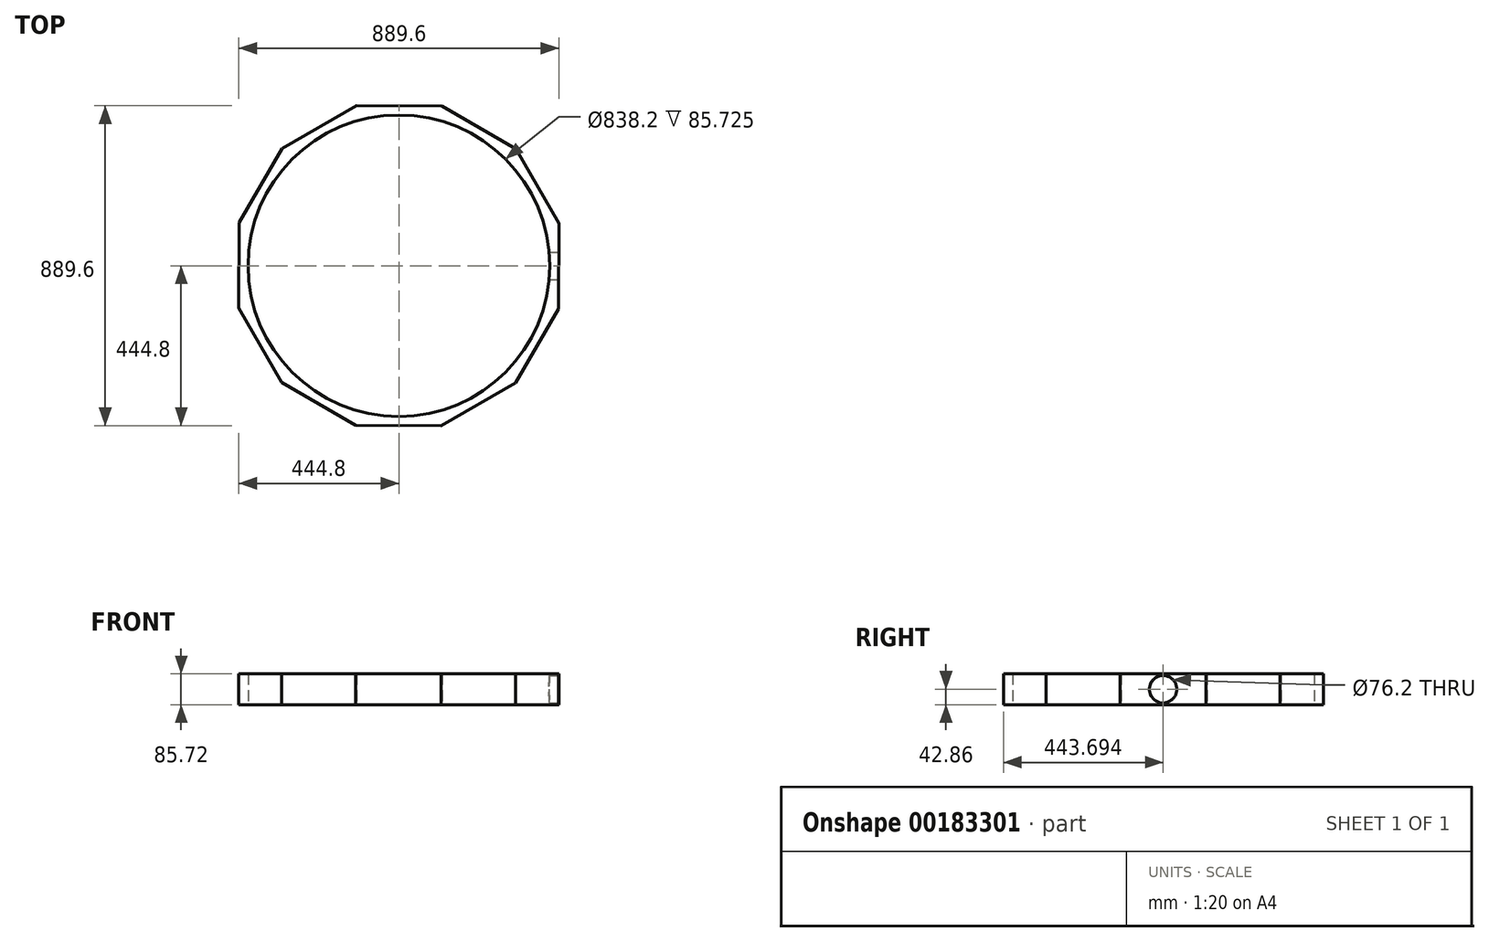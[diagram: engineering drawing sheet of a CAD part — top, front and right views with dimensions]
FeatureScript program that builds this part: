
annotation { "Feature Type Name" : "Feature", "Feature Type Description" : "" }
export const myFeature = defineFeature(function(context is Context, id is Id, definition is map)
    precondition{}
    {
        {
            var Q0;
            Q0=qCreatedBy(makeId("Top.planeOp"),FACE);
            var sketch = newSketch(context, id + "F0", { "sketchPlane" : qUnion([Q0])});
            skCircle(sketch, "E0.cCircle", {"center": v(0, 0) * mm, "radius": 444.5 * mm, "construction": true});
            skLineSegment(sketch, "E0.0", {"start": v(326.23, 324.56) * mm, "end": v(444.8, 117.97) * mm});
            skLineSegment(sketch, "E0.1", {"start": v(444.8, 117.97) * mm, "end": v(444.2, -120.24) * mm});
            skLineSegment(sketch, "E0.2", {"start": v(444.2, -120.24) * mm, "end": v(324.56, -326.23) * mm});
            skLineSegment(sketch, "E0.3", {"start": v(324.56, -326.23) * mm, "end": v(117.97, -444.8) * mm});
            skLineSegment(sketch, "E0.4", {"start": v(117.97, -444.8) * mm, "end": v(-120.24, -444.2) * mm});
            skLineSegment(sketch, "E0.5", {"start": v(-120.24, -444.2) * mm, "end": v(-326.23, -324.56) * mm});
            skLineSegment(sketch, "E0.6", {"start": v(-326.23, -324.56) * mm, "end": v(-444.8, -117.97) * mm});
            skLineSegment(sketch, "E0.7", {"start": v(-444.8, -117.97) * mm, "end": v(-444.2, 120.24) * mm});
            skLineSegment(sketch, "E0.8", {"start": v(-444.2, 120.24) * mm, "end": v(-324.56, 326.23) * mm});
            skLineSegment(sketch, "E0.9", {"start": v(-324.56, 326.23) * mm, "end": v(-117.97, 444.8) * mm});
            skLineSegment(sketch, "E0.10", {"start": v(-117.97, 444.8) * mm, "end": v(120.24, 444.2) * mm});
            skLineSegment(sketch, "E0.11", {"start": v(120.24, 444.2) * mm, "end": v(326.23, 324.56) * mm});
            skPoint(sketch, "E0.0.midPoint", {"position": v(385.52, 221.26) * mm});
            skCircle(sketch, "E1", {"center": v(0, 0) * mm, "radius": 419.1 * mm});
            skSolve(sketch);
        }
        {
            var Q0;
            Q0=makeQuery(id+"F0.imprint","IMPRINT",FACE,{"disambiguationData":[TD([[makeQuery(id+"F0.imprint","IMPRINT",EDGE,{"derivedFrom":sQuery(id+"F0.wireOp",EDGE,"E0.0")}),-1.0]])]});
            extrude(context, id + "F1", {"entities" : qUnion([Q0]), "endBound" : BoundingType.SYMMETRIC, "depth" : 85.72 * mm});
        }
        {
            var Q0;
            Q0=makeQuery(id+"F1.opExtrude","SWEPT_FACE",FACE,{"disambiguationData":[OSD([sQuery(id+"F0.wireOp",EDGE,"E0.1")])]});
            var sketch = newSketch(context, id + "F2", { "sketchPlane" : qUnion([Q0])});
            skCircle(sketch, "E2", {"center": v(0, 0) * mm, "radius": 38.1 * mm});
            skSolve(sketch);
        }
        {
            var Q0;
            Q0 = qSketchRegion(id + "F2", true);
            extrude(context, id + "F3", {"entities" : qUnion([Q0]), "operationType" : NewBodyOperationType.REMOVE, "oppositeDirection" : true, "depth" : 101.6 * mm});
        }
    });
